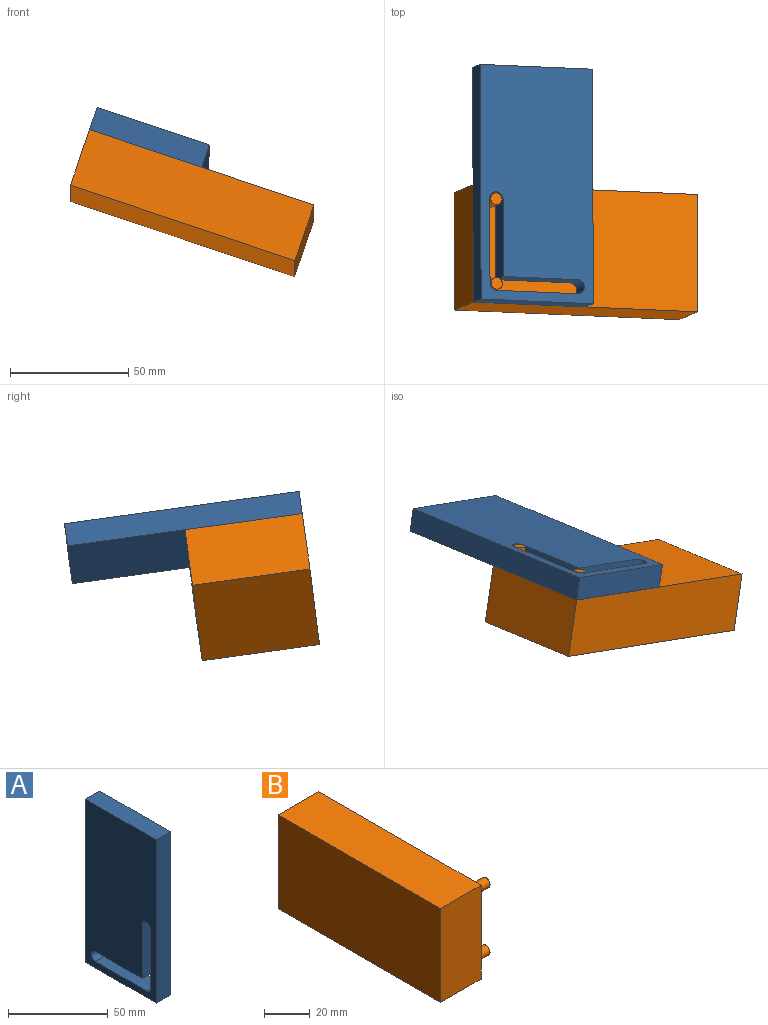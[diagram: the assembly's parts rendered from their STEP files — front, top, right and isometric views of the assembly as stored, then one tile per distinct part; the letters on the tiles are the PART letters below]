
ASSEMBLY  parts=2 mates=2
PART A: 13 faces, bbox 10x50x100 mm
  f0: plane 36x10mm, normal (0,0,1), area 360mm2, adj f1,f10,f11,f12
  f1: cylinder r=3mm len=10mm, axis (-1,0,0), area 47.1mm2, adj f0,f2,f11,f12
  f2: plane 36x10mm, normal (0,1,0), area 360mm2, adj f1,f3,f11,f12
  f3: cylinder r=3mm len=10mm, axis (-1,0,0), area 94.2mm2, adj f2,f4,f11,f12
  f4: plane 33x10mm, normal (0,-1,0), area 330mm2, adj f3,f5,f11,f12
  f5: plane 33x10mm, normal (0,0,-1), area 330mm2, adj f4,f10,f11,f12
  f6: plane 100x10mm, normal (0,-1,0), area 1000mm2, adj f7,f9,f11,f12
  f7: plane 50x10mm, normal (0,0,-1), area 500mm2, adj f6,f8,f11,f12
  f8: plane 100x10mm, normal (0,1,0), area 1000mm2, adj f7,f9,f11,f12
  f9: plane 50x10mm, normal (0,0,1), area 500mm2, adj f6,f8,f11,f12
  f10: cylinder r=3mm len=10mm, axis (-1,0,0), area 94.2mm2, adj f0,f5,f11,f12
  f11: plane 100x50mm, normal (1,0,0), area 4541.7mm2, adj f0,f1,f2,f3,f4,f5,f6,f7
  f12: plane 100x50mm, normal (-1,0,0), area 4541.7mm2, adj f0,f1,f2,f3,f4,f5,f6,f7
PART B: 10 faces, bbox 35x100x50 mm
  f0: plane 100x25mm, normal (0,0,1), area 2500mm2, adj f1,f3,f4,f5
  f1: plane 50x25mm, normal (0,-1,0), area 1250mm2, adj f0,f2,f4,f5
  f2: plane 100x25mm, normal (0,0,-1), area 2500mm2, adj f1,f3,f4,f5
  f3: plane 50x25mm, normal (0,1,0), area 1250mm2, adj f0,f2,f4,f5
  f4: plane 100x50mm, normal (-1,0,0), area 5000mm2, adj f0,f1,f2,f3
  f5: plane 100x50mm, normal (1,0,0), area 4960.7mm2, adj f0,f1,f2,f3,f6,f8
  f6: cylinder r=2.5mm len=10mm, axis (-1,0,0), area 157.1mm2, adj f5,f7
  f7: plane 5x5mm, normal (1,0,0), area 19.6mm2, adj f6
  f8: cylinder r=2.5mm len=10mm, axis (-1,0,0), area 157.1mm2, adj f5,f9
  f9: plane 5x5mm, normal (1,0,0), area 19.6mm2, adj f8
PLACE A rot(axis=(-0.72,-0.52,-0.45),115.4deg) t=(57.1,-36.42,128.62)mm fixed
PLACE B rot(axis=(-0.72,-0.52,-0.45),115.4deg) t=(57.1,-36.42,128.62)mm
MATE pin_slot B.f8 <-> A.f10  axis (0.32,0.13,0.94) through (63.7,-29.77,125.44)mm
MATE pin_slot B.f6 <-> A.f3  axis (0.32,0.13,0.94) through (63.56,5.9,120.51)mm
